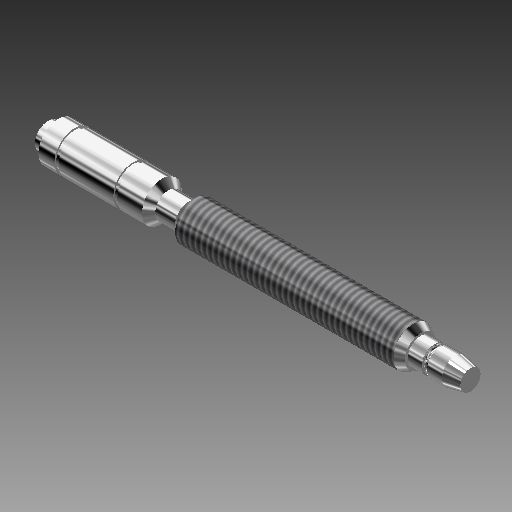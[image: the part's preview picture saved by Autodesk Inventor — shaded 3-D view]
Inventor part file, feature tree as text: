
AUTODESK INVENTOR PART (.ipt)
format: ipt  version: 2019 (Build 230136000, 136)  size: 220,672 bytes
history: native  units: mm
features: other x6, chamfer x4, revolve x2, sketch x2, extrude x1, thread x1
ambient origin geometry x6: Origin, XZ Plane, XY Plane, X Axis, Y Axis, Z Axis
bodies: Solid1 (feature_tree)
feature tree (16):
  revolve  "Revolution1"  [1 undecoded]
  other  "iFeature27:3"
  other  "iFeature27:2"
  other  "iFeature1:1"
  chamfer  "Chamfer4"  Distance=8.0mm
  chamfer  "Chamfer1"  Distance=12.0mm
  chamfer  "Chamfer2"  Distance=8.0mm
  chamfer  "Chamfer3"  Distance=12.0mm
  extrude  "Extrusion1"  TaperAngle=0.0deg  [1 undecoded]
  revolve  "Revolution2"  Angle=45.0deg
  thread  "Thread1"  [1 undecoded]
  other  "Start Plane"
  other  "Origin point"
  other  "Main Sketch"
  sketch  "Sketch3"  dims[d0=0.0mm d1=0.0mm]
  sketch  "Sketch4"  dims[d2=0.0mm d3=8.0mm d4=12.0mm d5=8.0mm d6=12.0mm d7=0.0mm d8=2.0mm d9=0.125mm d10=45.0deg d11=2.0mm d12=0.125mm d13=45.0deg d14=2.25mm d15=0.125mm d16=30.0deg d17=8.0mm d18=4.66mm d19=0.93mm d20=45.0deg d21=5.0mm d22=10.0mm d23=0.0mm d24=2.0mm d25=90.0deg d26=10.0mm d27=0.0mm]
note: 3 required parameter values undecoded (feature->parameter linkage not recoverable at this tier; creation-order binding heuristic only, values carry confidence <= 0.55)